# Revit family: r2018_videomax_server_OPS-SKUD_stoechnogo_ispolneniya
name_source: partatom
category: Устройства связи
revit_build: Autodesk Revit 2018 (Build: 20181011_1500(x64)
units: mm (PartAtom-declared; Revit-internal decimal feet)

## family parameters
Общий = Нет
Основа = Грань
При загрузке вырезать с полостями = Нет
Размер круглого соединителя = Использовать диаметр
Сохранять ориентацию аннотаций = Да
Тип детали = Нормальный
Точка расчета площади = Нет

## types (1)
- 19” 2U (2S)
    ADSK_Версия Revit = 2018
    ADSK_Версия семейства = v2
    ADSK_Единица измерения = шт.
    ADSK_Завод-изготовитель = ООО «Видеомакс»
    ADSK_Код изделия = ТУ 26.20.13-005-37165186-2018
    ADSK_Количество = 1
    ADSK_Коэффициент мощности = 0.96
    ADSK_Марка = VIDEOMAX-SB
    ADSK_Масса = 0
    ADSK_Наименование = Cервер ОПС-СКУД стоечного исполнения 19” 2U (2S)
    ADSK_Напряжение = 230 В
    ADSK_Номинальная мощность = 0 В·А
    ADSK_Обозначение = 19” 2U (2S)
    ADSK_Ток = 0 А
    Material = Черный
    URL = https://www.videomax-server.ru
    Высота = 88 мм
    Высота в U = 2
    Глубина = 430 мм
    Изготовитель = ООО «Видеомакс»
    Изображение типоразмера = 19 (2U.2S).png
    Количество COM-портов, шт. = 2
    Количество USB-портов, шт. = 2
    Количество входов 230V, шт = 0
    Количество интерфейсов Gigabit LAN, шт = 1
    Максимальная мощность БП, Вт = 0
    Максимальная потребляемая мощность Вт = 0
    Максимальное тепловыделение, BTU/h = 0
    Минимальная глубина шкафа, мм = 600
    Отметка по умолчанию = 2600 мм
    Стоимость = 0 $
    Тип линейки = Standart
    Указания по монтажу = Для монтажа использовать 19” салазки. Изделие комплектуется салазками SR20 либо SR26. Параметры SR20: расстояние между профилями 488 - 546 мм, габариты в сложенном состоянии 500 мм, параметры SR26: расстояние между профилями 572 - 672 мм, габариты в сложенном состоянии 650 мм.
    Ширина = 430 мм
